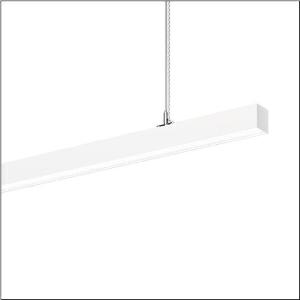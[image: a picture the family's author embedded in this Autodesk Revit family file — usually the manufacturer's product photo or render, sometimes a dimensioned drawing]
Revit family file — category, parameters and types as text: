
# Revit family: silica_r__21_51mx33tctdw_01d4
name_source: partatom
category: Lighting Fixtures
units: mm (PartAtom-declared; Revit-internal decimal feet)

## family parameters
Cut with Voids When Loaded = No
Host = Face
Light Source = No
Part Type = Normal
Room Calculation Point = No
Round Connector Dimension = Use Diameter
Shared = No

## types (1)
- --- (1 x LED, 14340 lm, 134.7 W, 6500K)
    Apparent Load = 135 VA
    CIE Flux Codes = 78 96 99 56 100
    Color Rendering = 80
    Color Temperature = 6500K
    Default Elevation = 1800 mm
    Description = Silica® 21, office luminaire, primary optical cover: prismatic diffuser, of PMMA, CAT 2 (L<= 3000cd/m²), light emission: direct/indirect distribution, primary light characteristic: symmetric, installation type: suspended mounting, LED, rated luminous flux: 14.340lm, luminous efficacy: 101lm/W, light colour: 8tw, colour temperature: 2700..6500K, control gear: ECG DALI, with terminal, 3+2-pole, max. 2.5mm², mains connection: 220..240V, AC, 50/60Hz, rated input power: 141.4W, luminaire housing, of aluminium, traffic white (RAL 9016), length: 3.004mm, width: 53mm, height: 53mm, protection rating (complete): IP20, insulation class (complete): insulation class I (protective earthing), certification: CE, permissible operating ambient temperature: 0..+35°C, standard: EN 50419, packaging unit: 1 piece
    Height = 53 mm
    Lamp = 1 x LED
    Lamp Light Flux = 14340 lm
    Lamp Power = 134.7 W
    Lamp count = 1
    Length = 3004 mm
    Luminous efficacy = 106 lm/W
    Manufacturer = Siteco
    ModVariant = No
    Model = 51MX33TCTDW
    Mounting Place = Ceiling
    Mounting Type = Pendant
    Number of Poles = 1
    OnlyDefault = Yes
    Power Factor = 1
    Product Name = Silica® 21
    Product group = office luminaire | ceiling pendant
    ProductGroupID = 902
    Protection Class = Protection class I
    Protection Degree = IP 20
    RLX_Detail_Level = 1
    RLX_Emergency_Light_Flux = 0 lm
    RLX_Emergency_Type = 0
    RLX_Emergency_Type_DB = No
    RlxData = <blob elided: 18101 chars, md5=70e64335>
    Socket = socket
    Standby Power = 0 W
    System Light Flux = 14340 lm
    System Power = 135 W
    Type Comments = individual setting
    Type Image = l_1297784.jpg
    URL = http://relux.com
    VarID = @adj_071095
    Voltage = 0 V
    Weight = 0.00 kg
    Width = 53 mm

## geometry (parser evidence)
native form markers: Blend x4, Sweep x13
no freeform markers — native parametric forms only
